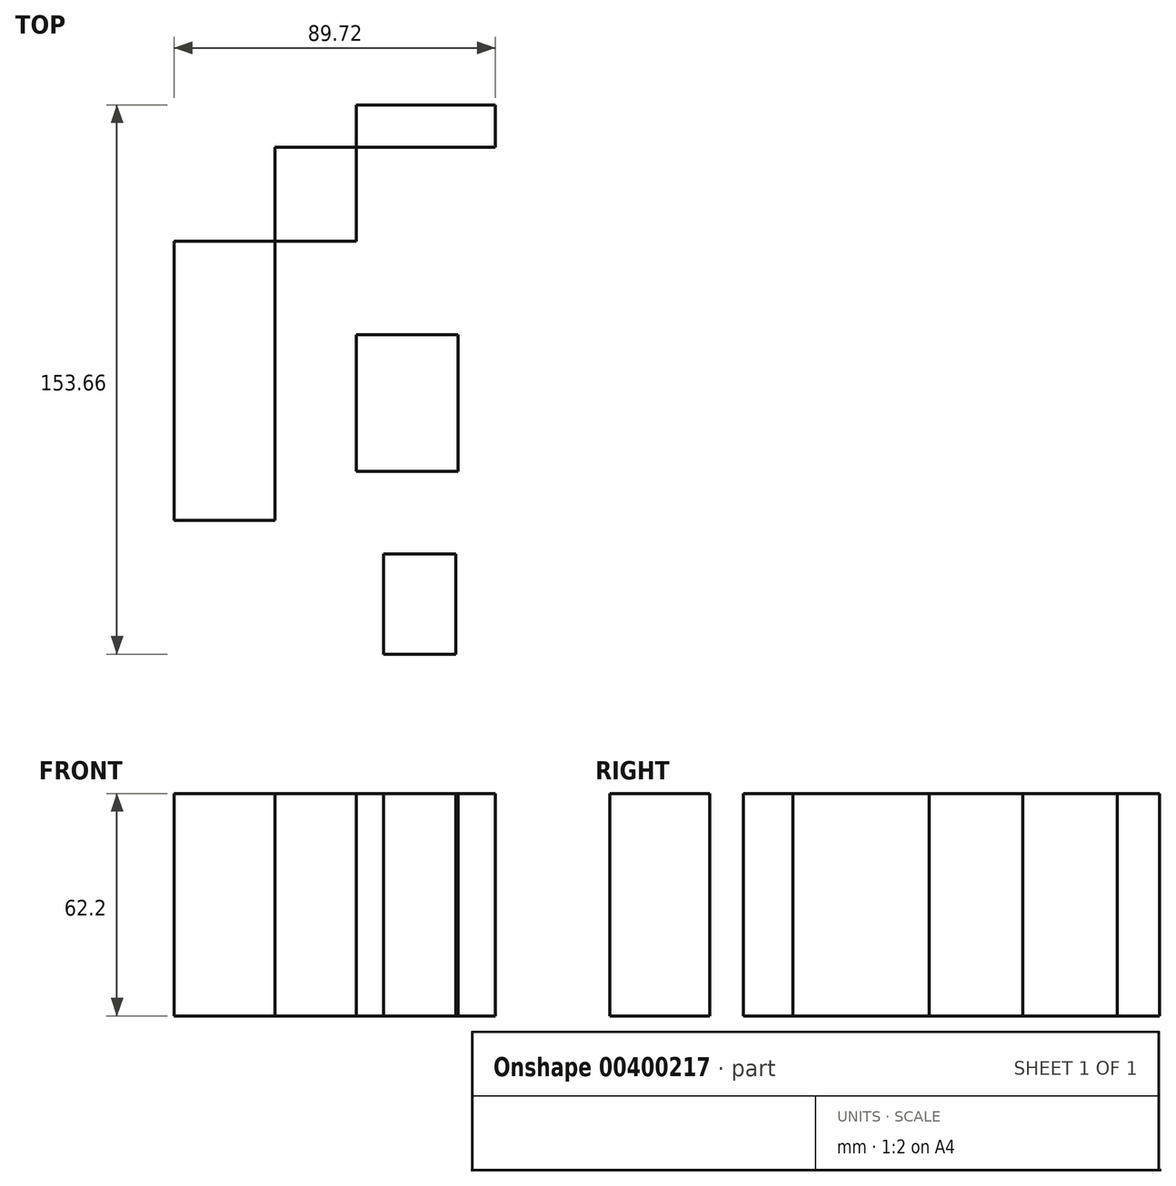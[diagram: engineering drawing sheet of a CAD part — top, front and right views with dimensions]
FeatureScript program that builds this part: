
annotation { "Feature Type Name" : "Feature", "Feature Type Description" : "" }
export const myFeature = defineFeature(function(context is Context, id is Id, definition is map)
    precondition{}
    {
        {
            var Q0;
            Q0=qCreatedBy(makeId("Top.planeOp"),FACE);
            var sketch = newSketch(context, id + "F0", { "sketchPlane" : qUnion([Q0])});
            skLineSegment(sketch, "E0.bottom", {"start": v(0, 64.33) * mm, "end": v(38.86, 64.33) * mm});
            skLineSegment(sketch, "E0.top", {"start": v(0, 52.55) * mm, "end": v(38.86, 52.55) * mm});
            skLineSegment(sketch, "E0.left", {"start": v(0, 64.33) * mm, "end": v(0, 52.55) * mm});
            skLineSegment(sketch, "E0.right", {"start": v(38.86, 64.33) * mm, "end": v(38.86, 52.55) * mm});
            skLineSegment(sketch, "E1.bottom", {"start": v(-22.67, 26.15) * mm, "end": v(0, 26.15) * mm});
            skLineSegment(sketch, "E1.top", {"start": v(-22.67, 52.55) * mm, "end": v(0, 52.55) * mm});
            skLineSegment(sketch, "E1.left", {"start": v(-22.67, 26.15) * mm, "end": v(-22.67, 52.55) * mm});
            skLineSegment(sketch, "E1.right", {"start": v(0, 26.15) * mm, "end": v(0, 52.55) * mm});
            skLineSegment(sketch, "E2.bottom", {"start": v(-22.67, 26.15) * mm, "end": v(-50.86, 26.15) * mm});
            skLineSegment(sketch, "E2.top", {"start": v(-22.67, -51.91) * mm, "end": v(-50.86, -51.91) * mm});
            skLineSegment(sketch, "E2.left", {"start": v(-22.67, 26.15) * mm, "end": v(-22.67, -51.91) * mm});
            skLineSegment(sketch, "E2.right", {"start": v(-50.86, 26.15) * mm, "end": v(-50.86, -51.91) * mm});
            skLineSegment(sketch, "E3.bottom", {"start": v(0, 0) * mm, "end": v(0, 0) * mm});
            skLineSegment(sketch, "E3.top", {"start": v(0, -38.15) * mm, "end": v(0, -38.15) * mm});
            skLineSegment(sketch, "E3.left", {"start": v(0, 0) * mm, "end": v(0, -38.15) * mm});
            skLineSegment(sketch, "E3.right", {"start": v(0, 0) * mm, "end": v(0, -38.15) * mm});
            skLineSegment(sketch, "E4.bottom", {"start": v(28.46, 0) * mm, "end": v(0, 0) * mm});
            skLineSegment(sketch, "E4.top", {"start": v(28.46, -38.15) * mm, "end": v(0, -38.15) * mm});
            skLineSegment(sketch, "E4.left", {"start": v(28.46, 0) * mm, "end": v(28.46, -38.15) * mm});
            skLineSegment(sketch, "E5.bottom", {"start": v(27.83, -89.33) * mm, "end": v(7.6, -89.33) * mm});
            skLineSegment(sketch, "E5.top", {"start": v(27.83, -61.33) * mm, "end": v(7.6, -61.33) * mm});
            skLineSegment(sketch, "E5.left", {"start": v(27.83, -89.33) * mm, "end": v(27.83, -61.33) * mm});
            skLineSegment(sketch, "E5.right", {"start": v(7.6, -89.33) * mm, "end": v(7.6, -61.33) * mm});
            skLineSegment(sketch, "E6.0", {"start": v(22.1, 0) * mm, "end": v(22.1, -38.15) * mm});
            skSolve(sketch);
        }
        {
            var Q0;
            Q0 = qSketchRegion(id + "F0", true);
            extrude(context, id + "F1", {"entities" : qUnion([Q0]), "depth" : 62.2 * mm});
        }
    });
